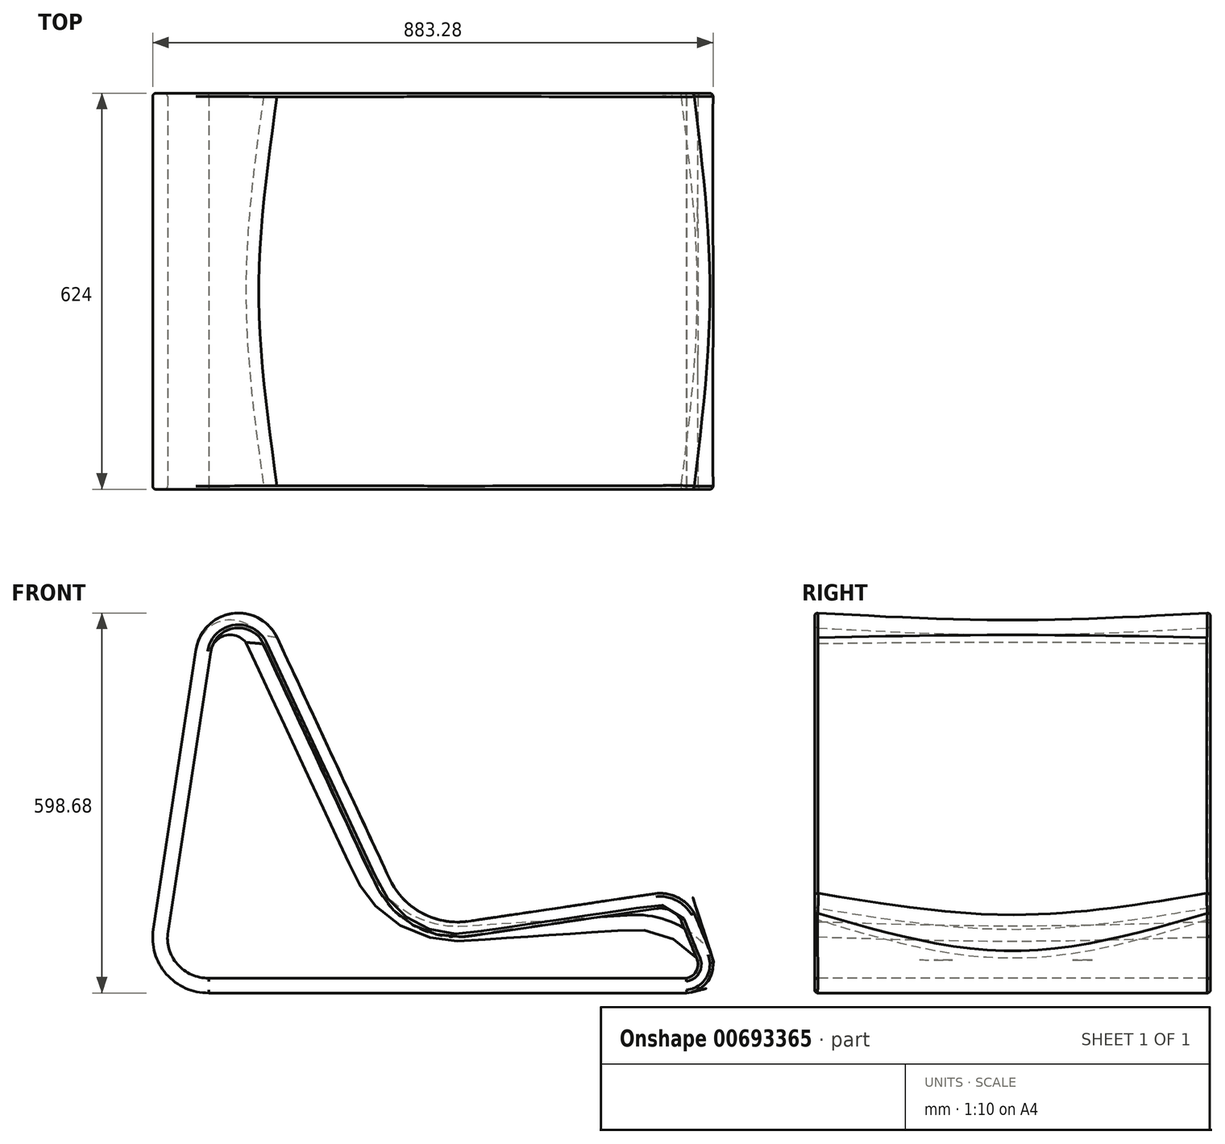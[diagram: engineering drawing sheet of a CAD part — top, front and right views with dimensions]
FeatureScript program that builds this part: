
annotation { "Feature Type Name" : "Feature", "Feature Type Description" : "" }
export const myFeature = defineFeature(function(context is Context, id is Id, definition is map)
    precondition{}
    {
        {
            var Q0;
            Q0=qCreatedBy(makeId("Front.planeOp"),FACE);
            var sketch = newSketch(context, id + "F0", { "sketchPlane" : qUnion([Q0])});
            skLineSegment(sketch, "E0", {"start": v(0, 0) * mm, "end": v(55, 0) * mm, "construction": true});
            skLineSegment(sketch, "E1", {"start": v(-4.73, 10.15) * mm, "end": v(-27.47, 58.91) * mm, "construction": true});
            skLineSegment(sketch, "E2", {"start": v(11.08, 1.66) * mm, "end": v(48.88, 7.32) * mm});
            skLineSegment(sketch, "E3", {"start": v(0, 0) * mm, "end": v(-27.47, 58.91) * mm});
            skPoint(sketch, "E4.visualSharp", {"position": v(0, 0) * mm});
            skArc(sketch, "E4.filletArc", {"start": v(-4.73, 10.15) * mm, "mid": v(1.76, 3.28) * mm, "end": v(11.08, 1.66) * mm});
            skLineSegment(sketch, "E5", {"start": v(55.2, -12.85) * mm, "end": v(-41.38, -12.85) * mm});
            skLineSegment(sketch, "E6", {"start": v(-52.59, 0) * mm, "end": v(-43.96, 56.54) * mm});
            skArc(sketch, "E7", {"start": v(-43.96, 56.54) * mm, "mid": v(-36.6, 63.85) * mm, "end": v(-27.47, 58.91) * mm});
            skArc(sketch, "E8", {"start": v(-52.59, 0) * mm, "mid": v(-49.96, -9.03) * mm, "end": v(-41.38, -12.85) * mm});
            skLineSegment(sketch, "E9", {"start": v(56.62, 3.45) * mm, "end": v(60.09, -4.9) * mm});
            skArc(sketch, "E10", {"start": v(60.09, -4.9) * mm, "mid": v(59.67, -10.13) * mm, "end": v(55.2, -12.85) * mm});
            skArc(sketch, "E11", {"start": v(48.88, 7.32) * mm, "mid": v(53.36, 6.6) * mm, "end": v(56.62, 3.45) * mm});
            skCircle(sketch, "E12", {"center": v(0, 0) * mm, "radius": 50 * mm, "construction": true});
            skSolve(sketch);
        }
        {
            var Q0;
            Q0=qCreatedBy(makeId("Front.planeOp"),FACE);
            cPlane(context, id + "F1", {"entities" : qUnion([Q0]), "cplaneType" : CPlaneType.OFFSET, "offset" : 40 * mm, "width" : 150 * mm, "height" : 150 * mm});
        }
        {
            var Q0;
            Q0=qCreatedBy(makeId("Front.planeOp"),FACE);
            cPlane(context, id + "F2", {"entities" : qUnion([Q0]), "cplaneType" : CPlaneType.OFFSET, "offset" : 80 * mm, "width" : 150 * mm, "height" : 150 * mm});
        }
        {
            var Q0;
            Q0=qCreatedBy(id+"F2.planeOp",FACE);
            var sketch = newSketch(context, id + "F3", { "sketchPlane" : qUnion([Q0])});
            skLineSegment(sketch, "E13", {"start": v(0, 0) * mm, "end": v(55, 0) * mm, "construction": true});
            skLineSegment(sketch, "E14", {"start": v(-4.73, 10.15) * mm, "end": v(-27.47, 58.91) * mm, "construction": true});
            skLineSegment(sketch, "E15", {"start": v(11.08, 1.66) * mm, "end": v(48.88, 7.32) * mm});
            skLineSegment(sketch, "E16", {"start": v(0, 0) * mm, "end": v(-27.47, 58.91) * mm});
            skPoint(sketch, "E17.visualSharp", {"position": v(0, 0) * mm});
            skArc(sketch, "E17.filletArc", {"start": v(-4.73, 10.15) * mm, "mid": v(1.76, 3.28) * mm, "end": v(11.08, 1.66) * mm});
            skLineSegment(sketch, "E18", {"start": v(55.2, -12.85) * mm, "end": v(-41.38, -12.85) * mm});
            skLineSegment(sketch, "E19", {"start": v(-52.59, 0) * mm, "end": v(-43.96, 56.54) * mm});
            skArc(sketch, "E20", {"start": v(-43.96, 56.54) * mm, "mid": v(-36.6, 63.85) * mm, "end": v(-27.47, 58.91) * mm});
            skArc(sketch, "E21", {"start": v(-52.59, 0) * mm, "mid": v(-49.96, -9.03) * mm, "end": v(-41.38, -12.85) * mm});
            skLineSegment(sketch, "E22", {"start": v(56.62, 3.45) * mm, "end": v(60.09, -4.9) * mm});
            skArc(sketch, "E23", {"start": v(60.09, -4.9) * mm, "mid": v(59.67, -10.13) * mm, "end": v(55.2, -12.85) * mm});
            skArc(sketch, "E24", {"start": v(48.88, 7.32) * mm, "mid": v(53.36, 6.6) * mm, "end": v(56.62, 3.45) * mm});
            skCircle(sketch, "E25", {"center": v(0, 0) * mm, "radius": 50 * mm, "construction": true});
            skSolve(sketch);
        }
        {
            var Q0;
            Q0=qCreatedBy(id+"F1.planeOp",FACE);
            var sketch = newSketch(context, id + "F4", { "sketchPlane" : qUnion([Q0])});
            skLineSegment(sketch, "E26", {"start": v(0, 0) * mm, "end": v(55, 0) * mm, "construction": true});
            skLineSegment(sketch, "E27", {"start": v(10.24, 0.68) * mm, "end": v(43.68, 2.89) * mm});
            skPoint(sketch, "E28.visualSharp", {"position": v(0, 0) * mm});
            skArc(sketch, "E28.filletArc", {"start": v(-9.2, 12.17) * mm, "mid": v(-1.26, 3.42) * mm, "end": v(10.24, 0.68) * mm});
            skLineSegment(sketch, "E29", {"start": v(55.2, -12.85) * mm, "end": v(-41.38, -12.85) * mm});
            skLineSegment(sketch, "E30", {"start": v(-52.59, 0) * mm, "end": v(-43.96, 56.54) * mm});
            skArc(sketch, "E31", {"start": v(-52.59, 0) * mm, "mid": v(-49.96, -9.03) * mm, "end": v(-41.38, -12.85) * mm});
            skLineSegment(sketch, "E32", {"start": v(59.9, -4.36) * mm, "end": v(60.17, -5.12) * mm});
            skArc(sketch, "E33", {"start": v(60.17, -5.12) * mm, "mid": v(59.61, -10.23) * mm, "end": v(55.2, -12.85) * mm});
            skArc(sketch, "E34", {"start": v(43.68, 2.89) * mm, "mid": v(52.68, 1.27) * mm, "end": v(59.9, -4.36) * mm});
            skCircle(sketch, "E35", {"center": v(0, 0) * mm, "radius": 50 * mm, "construction": true});
            skLineSegment(sketch, "E36", {"start": v(-9.2, 12.17) * mm, "end": v(-31.28, 59.48) * mm});
            skArc(sketch, "E37", {"start": v(-43.96, 56.54) * mm, "mid": v(-38.62, 62.31) * mm, "end": v(-31.28, 59.48) * mm});
            skSolve(sketch);
        }
        {
            var Q0;
            Q0=makeQuery(id+"F0.imprint","IMPRINT",FACE,{"disambiguationData":[TD([[makeQuery(id+"F0.imprint","IMPRINT",EDGE,{"derivedFrom":sQuery(id+"F0.wireOp",EDGE,"E2")}),-1.0]])]});
            var Q1;
            Q1=makeQuery(id+"F4.imprint","IMPRINT",FACE,{"disambiguationData":[TD([[makeQuery(id+"F4.imprint","IMPRINT",EDGE,{"derivedFrom":sQuery(id+"F4.wireOp",EDGE,"E27")}),-1.0]])]});
            var Q2;
            Q2=makeQuery(id+"F3.imprint","IMPRINT",FACE,{"disambiguationData":[TD([[makeQuery(id+"F3.imprint","IMPRINT",EDGE,{"derivedFrom":sQuery(id+"F3.wireOp",EDGE,"E15")}),-1.0]])]});
            loft(context, id + "F5", {"sheetProfilesArray" : [{ "sheetProfileEntities" : qUnion([Q0]) }, { "sheetProfileEntities" : qUnion([Q1]) }, { "sheetProfileEntities" : qUnion([Q2]) }]});
        }
        {
            var Q0;
            Q0=makeQuery(id+"F5.opLoft","CAP_FACE",FACE,{"disambiguationData":[OSD([makeQuery(id+"F3.imprint","IMPRINT",FACE,{"disambiguationData":[TD([[makeQuery(id+"F3.imprint","IMPRINT",EDGE,{"derivedFrom":sQuery(id+"F3.wireOp",EDGE,"E15")}),-1.0]])]})])],"isStart":true});
            var Q1;
            Q1=makeQuery(id+"F5.opLoft","CAP_FACE",FACE,{"disambiguationData":[OSD([makeQuery(id+"F0.imprint","IMPRINT",FACE,{"disambiguationData":[TD([[makeQuery(id+"F0.imprint","IMPRINT",EDGE,{"derivedFrom":sQuery(id+"F0.wireOp",EDGE,"E2")}),-1.0]])]})])],"isStart":true});
            shell(context, id + "F6", {"entities" : qUnion([Q0, Q1]), "thickness" : 3 * mm});
        }
        {
            var Q0;
            Q0=makeQuery(id+"F5.opLoft","SWEPT_BODY",BODY,{"disambiguationData":[OSD([makeQuery(id+"F0.imprint","IMPRINT",FACE,{"disambiguationData":[TD([[makeQuery(id+"F0.imprint","IMPRINT",EDGE,{"derivedFrom":sQuery(id+"F0.wireOp",EDGE,"E2")}),-1.0]])]}),makeQuery(id+"F3.imprint","IMPRINT",FACE,{"disambiguationData":[TD([[makeQuery(id+"F3.imprint","IMPRINT",EDGE,{"derivedFrom":sQuery(id+"F3.wireOp",EDGE,"E15")}),-1.0]])]}),sQuery(id+"F4.wireOp",EDGE,"E30")])]});
            var Q1;
            Q1=sQuery(id+"F0.wireOp",VERTEX,"E4.visualSharp");
            transform(context, id + "F7", {"entities" : qUnion([Q0]), "transformType" : TransformType.SCALE_UNIFORMLY, "scale" : 0.78, "scalePoint" : qUnion([Q1]), "makeCopy" : false});
        }
        {
            var Q0;
            Q0=makeQuery(id+"F5.opLoft","CAP_FACE",FACE,{"disambiguationData":[OSD([makeQuery(id+"F3.imprint","IMPRINT",FACE,{"disambiguationData":[TD([[makeQuery(id+"F3.imprint","IMPRINT",EDGE,{"derivedFrom":sQuery(id+"F3.wireOp",EDGE,"E15")}),-1.0]])]})])],"isStart":true});
            var Q1;
            Q1=makeQuery(id+"F5.opLoft","CAP_FACE",FACE,{"disambiguationData":[OSD([makeQuery(id+"F0.imprint","IMPRINT",FACE,{"disambiguationData":[TD([[makeQuery(id+"F0.imprint","IMPRINT",EDGE,{"derivedFrom":sQuery(id+"F0.wireOp",EDGE,"E2")}),-1.0]])]})])],"isStart":true});
            fillet(context, id + "F8", {"entities" : qUnion([Q0, Q1]), "radius" : 0.5 * mm, "tangentPropagation" : true, "allowEdgeOverflow" : false});
        }
        {
            var Q0;
            Q0=makeQuery(id+"F5.opLoft","SWEPT_BODY",BODY,{"disambiguationData":[OSD([makeQuery(id+"F0.imprint","IMPRINT",FACE,{"disambiguationData":[TD([[makeQuery(id+"F0.imprint","IMPRINT",EDGE,{"derivedFrom":sQuery(id+"F0.wireOp",EDGE,"E2")}),-1.0]])]}),makeQuery(id+"F3.imprint","IMPRINT",FACE,{"disambiguationData":[TD([[makeQuery(id+"F3.imprint","IMPRINT",EDGE,{"derivedFrom":sQuery(id+"F3.wireOp",EDGE,"E15")}),-1.0]])]}),sQuery(id+"F4.wireOp",EDGE,"E30")])]});
            var Q1;
            Q1=sQuery(id+"F0.wireOp",VERTEX,"E4.visualSharp");
            transform(context, id + "F9", {"entities" : qUnion([Q0]), "transformType" : TransformType.SCALE_UNIFORMLY, "scale" : 10, "scalePoint" : qUnion([Q1]), "makeCopy" : false});
        }
    });
